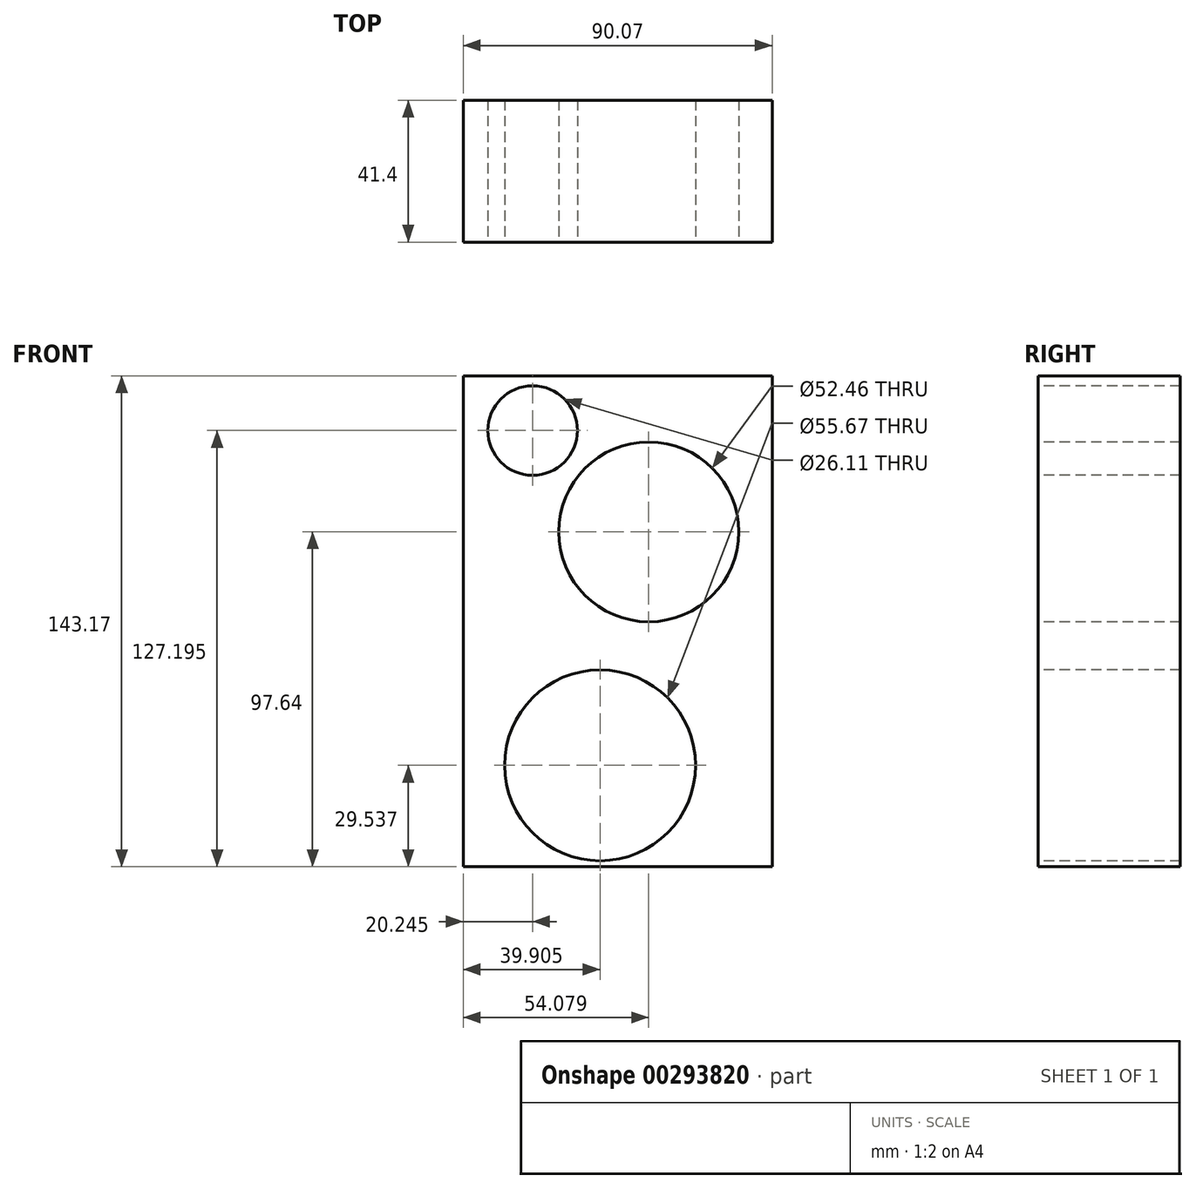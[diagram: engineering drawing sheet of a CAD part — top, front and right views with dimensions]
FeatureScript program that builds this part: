
annotation { "Feature Type Name" : "Feature", "Feature Type Description" : "" }
export const myFeature = defineFeature(function(context is Context, id is Id, definition is map)
    precondition{}
    {
        {
            var Q0;
            Q0=qCreatedBy(makeId("Front.planeOp"),FACE);
            var sketch = newSketch(context, id + "F0", { "sketchPlane" : qUnion([Q0])});
            skLineSegment(sketch, "E0.bottom", {"start": v(-67.44, 64.66) * mm, "end": v(22.63, 64.66) * mm});
            skLineSegment(sketch, "E0.top", {"start": v(-67.44, -78.51) * mm, "end": v(22.63, -78.51) * mm});
            skLineSegment(sketch, "E0.left", {"start": v(-67.44, 64.66) * mm, "end": v(-67.44, -78.51) * mm});
            skLineSegment(sketch, "E0.right", {"start": v(22.63, 64.66) * mm, "end": v(22.63, -78.51) * mm});
            skSolve(sketch);
        }
        {
            var Q0;
            Q0=makeQuery(id+"F0.imprint","IMPRINT",FACE,{"disambiguationData":[TD([[makeQuery(id+"F0.imprint","IMPRINT",EDGE,{"derivedFrom":sQuery(id+"F0.wireOp",EDGE,"E0.bottom")}),-1.0]])]});
            extrude(context, id + "F1", {"entities" : qUnion([Q0]), "depth" : 41.4 * mm});
        }
        {
            var Q0;
            Q0=makeQuery(id+"F1.opExtrude","CAP_FACE",FACE,{"disambiguationData":[OSD([sQuery(id+"F0.wireOp",EDGE,"E0.bottom"),sQuery(id+"F0.wireOp",EDGE,"E0.top"),sQuery(id+"F0.wireOp",EDGE,"E0.left"),sQuery(id+"F0.wireOp",EDGE,"E0.right")])],"isStart":false});
            var sketch = newSketch(context, id + "F2", { "sketchPlane" : qUnion([Q0])});
            skCircle(sketch, "E1", {"center": v(-47.2, 48.68) * mm, "radius": 13.05 * mm});
            skCircle(sketch, "E2", {"center": v(-13.36, 19.13) * mm, "radius": 26.23 * mm});
            skCircle(sketch, "E3", {"center": v(-27.53, -48.97) * mm, "radius": 27.83 * mm});
            skSolve(sketch);
        }
        {
            var Q0;
            Q0=makeQuery(id+"F2.imprint","IMPRINT",FACE,{"disambiguationData":[TD([[makeQuery(id+"F2.imprint","IMPRINT",EDGE,{"derivedFrom":sQuery(id+"F2.wireOp",EDGE,"E2")}),1.0]])]});
            var Q1;
            Q1=makeQuery(id+"F2.imprint","IMPRINT",FACE,{"disambiguationData":[TD([[makeQuery(id+"F2.imprint","IMPRINT",EDGE,{"derivedFrom":sQuery(id+"F2.wireOp",EDGE,"E3")}),1.0]])]});
            var Q2;
            Q2=makeQuery(id+"F2.imprint","IMPRINT",FACE,{"disambiguationData":[TD([[makeQuery(id+"F2.imprint","IMPRINT",EDGE,{"derivedFrom":sQuery(id+"F2.wireOp",EDGE,"E1")}),1.0]])]});
            extrude(context, id + "F3", {"entities" : qUnion([Q0, Q1, Q2]), "operationType" : NewBodyOperationType.REMOVE, "oppositeDirection" : true, "depth" : 57.15 * mm});
        }
    });
